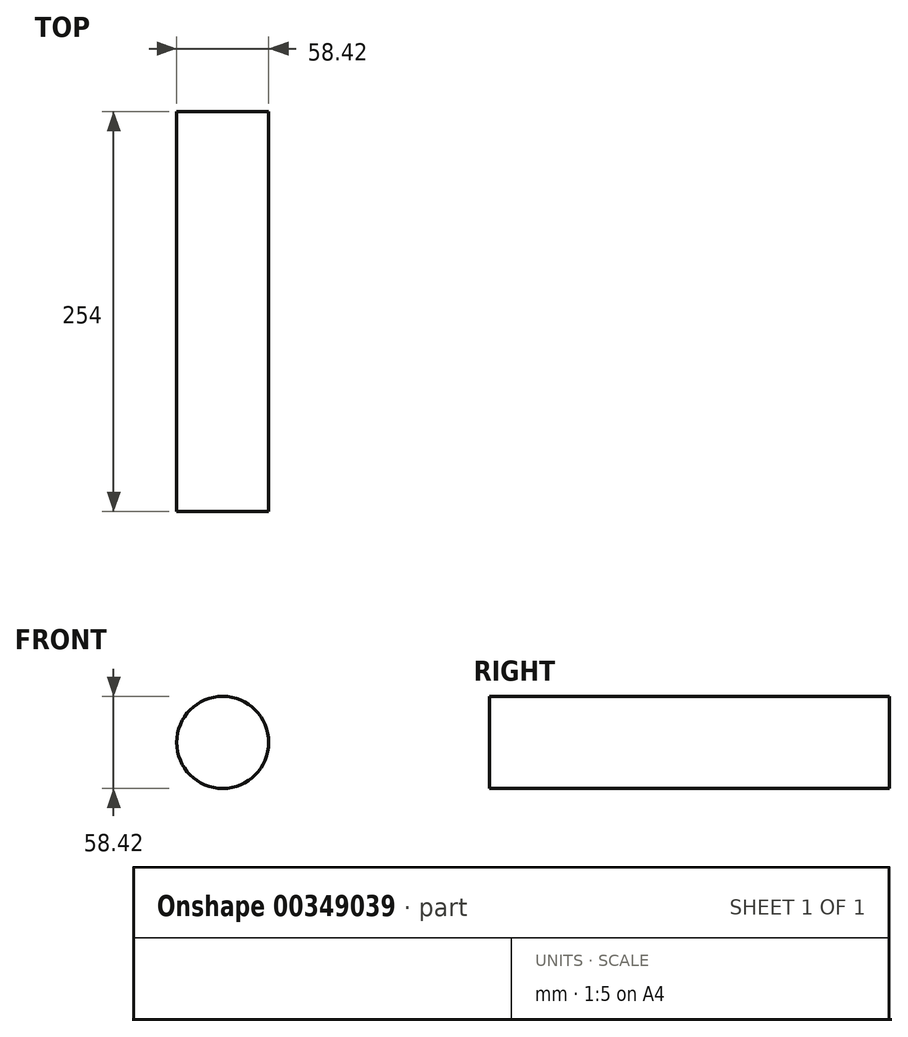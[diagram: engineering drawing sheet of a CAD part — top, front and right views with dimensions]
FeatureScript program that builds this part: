
annotation { "Feature Type Name" : "Feature", "Feature Type Description" : "" }
export const myFeature = defineFeature(function(context is Context, id is Id, definition is map)
    precondition{}
    {
        {
            var Q0;
            Q0=qCreatedBy(makeId("Front.planeOp"),FACE);
            var sketch = newSketch(context, id + "F0", { "sketchPlane" : qUnion([Q0])});
            skCircle(sketch, "E0", {"center": v(0, 0) * mm, "radius": 29.2 * mm});
            skSolve(sketch);
        }
        {
            var Q0;
            Q0=makeQuery(id+"F0.imprint","IMPRINT",FACE,{"disambiguationData":[TD([[makeQuery(id+"F0.imprint","IMPRINT",EDGE,{"derivedFrom":sQuery(id+"F0.wireOp",EDGE,"E0")}),1.0]])]});
            extrude(context, id + "F1", {"entities" : qUnion([Q0]), "endBound" : BoundingType.SYMMETRIC, "depth" : 254 * mm});
        }
    });
